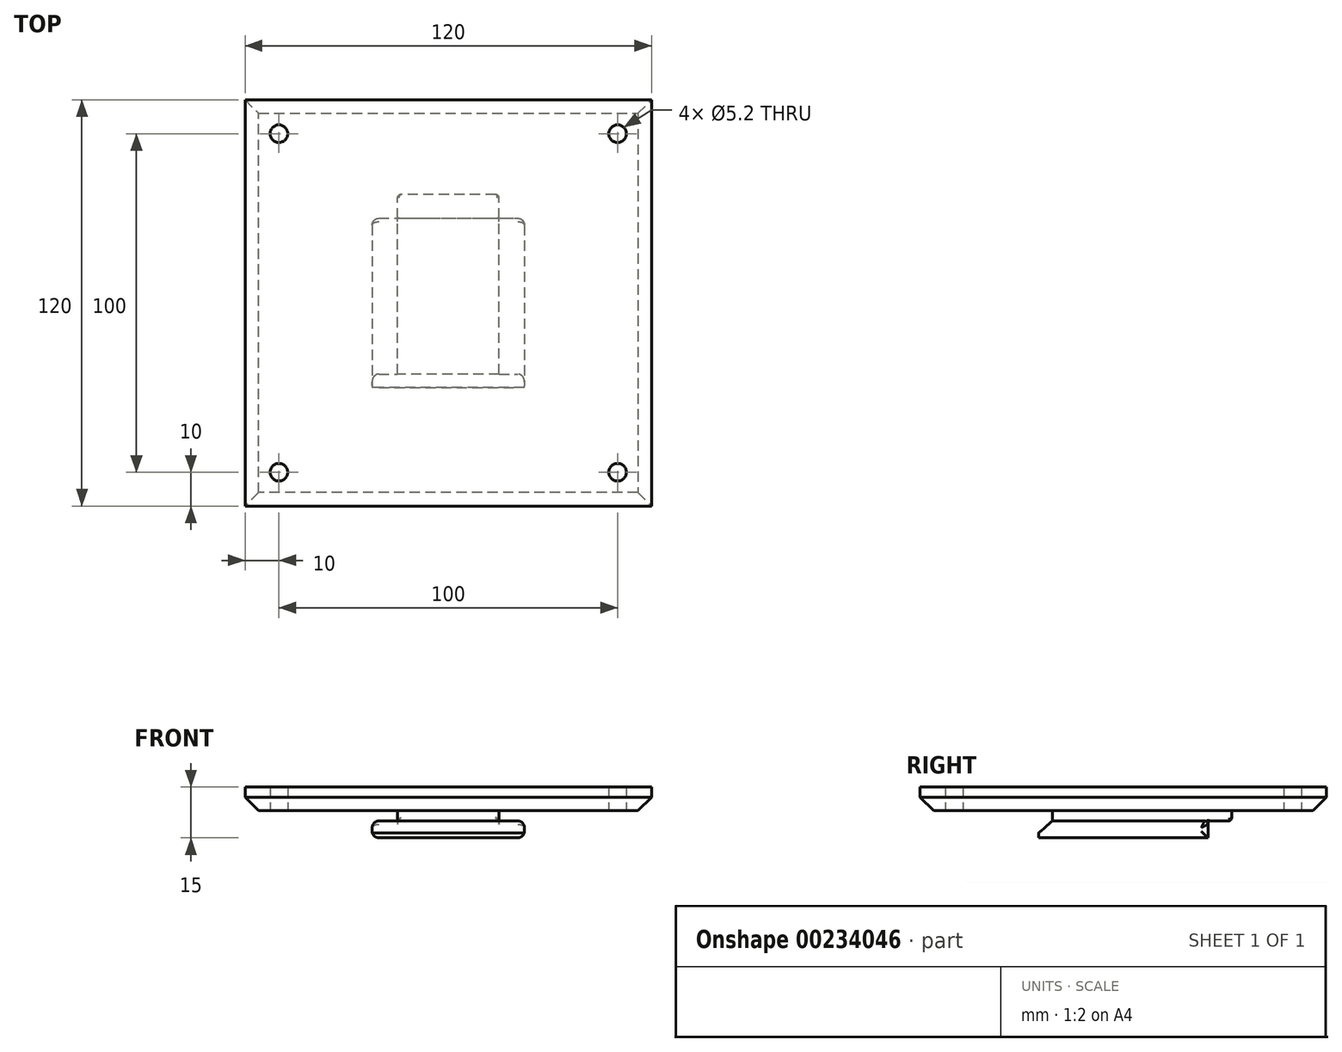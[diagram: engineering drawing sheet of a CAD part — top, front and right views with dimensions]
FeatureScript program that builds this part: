
annotation { "Feature Type Name" : "Feature", "Feature Type Description" : "" }
export const myFeature = defineFeature(function(context is Context, id is Id, definition is map)
    precondition{}
    {
        {
            var Q0;
            Q0=qCreatedBy(makeId("Top.planeOp"),FACE);
            var sketch = newSketch(context, id + "F0", { "sketchPlane" : qUnion([Q0])});
            skLineSegment(sketch, "E0.bottom", {"start": v(-45, 50) * mm, "end": v(0, 50) * mm});
            skLineSegment(sketch, "E0.top", {"start": v(-45, 0) * mm, "end": v(0, 0) * mm});
            skLineSegment(sketch, "E0.left", {"start": v(-45, 50) * mm, "end": v(-45, 0) * mm});
            skLineSegment(sketch, "E0.right", {"start": v(0, 50) * mm, "end": v(0, 0) * mm});
            skSolve(sketch);
        }
        {
            var Q0;
            Q0=makeQuery(id+"F0.imprint","IMPRINT",FACE,{"disambiguationData":[TD([[makeQuery(id+"F0.imprint","IMPRINT",EDGE,{"derivedFrom":sQuery(id+"F0.wireOp",EDGE,"E0.bottom")}),-1.0]])]});
            extrude(context, id + "F1", {"entities" : qUnion([Q0]), "depth" : 5 * mm});
        }
        {
            var Q0;
            Q0=makeQuery(id+"F1.opExtrude","CAP_FACE",FACE,{"disambiguationData":[OSD([sQuery(id+"F0.wireOp",EDGE,"E0.bottom"),sQuery(id+"F0.wireOp",EDGE,"E0.top"),sQuery(id+"F0.wireOp",EDGE,"E0.left"),sQuery(id+"F0.wireOp",EDGE,"E0.right")])],"isStart":false});
            var sketch = newSketch(context, id + "F2", { "sketchPlane" : qUnion([Q0])});
            skLineSegment(sketch, "E1.bottom", {"start": v(-7.5, 4) * mm, "end": v(-37.5, 4) * mm});
            skLineSegment(sketch, "E1.top", {"start": v(-7.5, 57) * mm, "end": v(-37.5, 57) * mm});
            skLineSegment(sketch, "E1.left", {"start": v(-7.5, 4) * mm, "end": v(-7.5, 57) * mm});
            skLineSegment(sketch, "E1.right", {"start": v(-37.5, 4) * mm, "end": v(-37.5, 57) * mm});
            skSolve(sketch);
        }
        {
            var Q0;
            {var subQ0=sQuery(id+"F2.wireOp",EDGE,"E1.top");Q0=makeQuery(id+"F2.imprint","IMPRINT",FACE,{"disambiguationData":[TD([[makeQuery(id+"F2.imprint","IMPRINT",EDGE,{"derivedFrom":subQ0}),1.0]])]});}
            var Q1;
            {var subQ0=sQuery(id+"F2.wireOp",EDGE,"E1.bottom");Q1=makeQuery(id+"F2.imprint","IMPRINT",FACE,{"disambiguationData":[TD([[makeQuery(id+"F2.imprint","IMPRINT",EDGE,{"derivedFrom":subQ0}),-1.0]])]});}
            extrude(context, id + "F3", {"entities" : qUnion([Q0, Q1]), "operationType" : NewBodyOperationType.ADD, "depth" : 3 * mm});
        }
        {
            var Q0;
            Q0=makeQuery(id+"F3.opExtrude","CAP_FACE",FACE,{"disambiguationData":[OSD([sQuery(id+"F2.wireOp",EDGE,"E1.bottom"),sQuery(id+"F2.wireOp",EDGE,"E1.top"),sQuery(id+"F2.wireOp",EDGE,"E1.left"),sQuery(id+"F2.wireOp",EDGE,"E1.right")])],"isStart":false});
            var sketch = newSketch(context, id + "F4", { "sketchPlane" : qUnion([Q0])});
            skLineSegment(sketch, "E2.bottom", {"start": v(-82.5, 85) * mm, "end": v(37.5, 85) * mm});
            skLineSegment(sketch, "E2.top", {"start": v(-82.5, -35) * mm, "end": v(37.5, -35) * mm});
            skLineSegment(sketch, "E2.left", {"start": v(-82.5, 85) * mm, "end": v(-82.5, -35) * mm});
            skLineSegment(sketch, "E2.right", {"start": v(37.5, 85) * mm, "end": v(37.5, -35) * mm});
            skLineSegment(sketch, "E3", {"start": v(-22.5, 85) * mm, "end": v(-22.5, -35) * mm, "construction": true});
            skLineSegment(sketch, "E4", {"start": v(-82.5, 25) * mm, "end": v(37.5, 25) * mm, "construction": true});
            skPoint(sketch, "E5", {"position": v(-22.5, 25) * mm});
            skLineSegment(sketch, "E6.bottom", {"start": v(27.5, 75) * mm, "end": v(-72.5, 75) * mm, "construction": true});
            skLineSegment(sketch, "E6.top", {"start": v(27.5, -25) * mm, "end": v(-72.5, -25) * mm, "construction": true});
            skLineSegment(sketch, "E6.left", {"start": v(27.5, 75) * mm, "end": v(27.5, -25) * mm, "construction": true});
            skLineSegment(sketch, "E6.right", {"start": v(-72.5, 75) * mm, "end": v(-72.5, -25) * mm, "construction": true});
            skPoint(sketch, "E7", {"position": v(-72.5, 75) * mm});
            skPoint(sketch, "E8", {"position": v(27.5, 75) * mm});
            skPoint(sketch, "E9", {"position": v(27.5, -25) * mm});
            skPoint(sketch, "E10", {"position": v(-72.5, -25) * mm});
            skSolve(sketch);
        }
        {
            var Q0;
            Q0=makeQuery(id+"F4.imprint","IMPRINT",FACE,{"disambiguationData":[TD([[makeQuery(id+"F4.imprint","IMPRINT",EDGE,{"derivedFrom":sQuery(id+"F4.wireOp",EDGE,"E2.bottom")}),-1.0]])]});
            var Q1;
            Q1=makeQuery(id+"F4.imprint","IMPRINT",FACE,{"disambiguationData":[TD([[makeQuery(id+"F4.imprint","IMPRINT",EDGE,{"derivedFrom":makeQuery(id+"F3.opExtrude","CAP_EDGE",EDGE,{"disambiguationData":[OSD([sQuery(id+"F2.wireOp",EDGE,"E1.bottom")])],"isStart":false})}),-1.0]])]});
            extrude(context, id + "F5", {"entities" : qUnion([Q0, Q1]), "operationType" : NewBodyOperationType.ADD, "depth" : 7 * mm});
        }
        {
            var Q0;
            Q0=sQuery(id+"F4.wireOp",VERTEX,"E10");
            var Q1;
            Q1=sQuery(id+"F4.wireOp",VERTEX,"E9");
            var Q2;
            Q2=sQuery(id+"F4.wireOp",VERTEX,"E8");
            var Q3;
            Q3=sQuery(id+"F4.wireOp",VERTEX,"E7");
            var Q4;
            Q4=makeQuery(id+"F1.opExtrude","SWEPT_BODY",BODY,{"disambiguationData":[OSD([sQuery(id+"F0.wireOp",EDGE,"E0.bottom"),sQuery(id+"F0.wireOp",EDGE,"E0.top"),sQuery(id+"F0.wireOp",EDGE,"E0.left"),sQuery(id+"F0.wireOp",EDGE,"E0.right")])]});
            hole(context, id + "F6", {"style" : HoleStyle.SIMPLE, "endStyle" : HoleEndStyle.THROUGH, "oppositeDirection" : true, "holeDiameter" : 5.2 * mm, "startFromSketch" : true, "locations" : qUnion([Q0, Q1, Q2, Q3]), "scope" : qUnion([Q4]), "isTappedThrough" : true});
        }
        {
            var Q0;
            Q0=makeQuery(id+"F1.opExtrude","CAP_EDGE",EDGE,{"disambiguationData":[OSD([sQuery(id+"F0.wireOp",EDGE,"E0.top")])],"isStart":false});
            chamfer(context, id + "F7", {"entities" : qUnion([Q0]), "chamferType" : ChamferType.TWO_OFFSETS, "width1" : 4 * mm, "oppositeDirection" : false, "width2" : 3.5 * mm, "tangentPropagation" : true});
        }
        {
            var Q0;
            Q0=makeQuery(id+"F3.opExtrude","CAP_EDGE",EDGE,{"disambiguationData":[OSD([sQuery(id+"F2.wireOp",EDGE,"E1.bottom")])],"isStart":false});
            var Q1;
            Q1=makeQuery(id+"F3.opExtrude","CAP_EDGE",EDGE,{"disambiguationData":[OSD([sQuery(id+"F2.wireOp",EDGE,"E1.right")])],"isStart":false});
            var Q2;
            Q2=makeQuery(id+"F3.opExtrude","CAP_EDGE",EDGE,{"disambiguationData":[OSD([sQuery(id+"F2.wireOp",EDGE,"E1.left")])],"isStart":false});
            var Q3;
            {var subQ0=sQuery(id+"F2.wireOp",EDGE,"E1.right");Q3=makeQuery(id+"F3.boolean.opBoolean","SPLIT",EDGE,{"disambiguationData":[topologyDisambiguationEdgeConnected([makeQuery(id+"F1.opExtrude","CAP_FACE",FACE,{"disambiguationData":[OSD([sQuery(id+"F0.wireOp",EDGE,"E0.bottom"),sQuery(id+"F0.wireOp",EDGE,"E0.top"),sQuery(id+"F0.wireOp",EDGE,"E0.left"),sQuery(id+"F0.wireOp",EDGE,"E0.right")])],"isStart":false})])],"derivedFrom":makeQuery(id+"F3.opExtrude","CAP_EDGE",EDGE,{"disambiguationData":[OSD([subQ0])],"isStart":true})});}
            var Q4;
            Q4=makeQuery(id+"F3.opExtrude","CAP_EDGE",EDGE,{"disambiguationData":[OSD([sQuery(id+"F2.wireOp",EDGE,"E1.top")])],"isStart":false});
            var Q5;
            {var subQ0=sQuery(id+"F2.wireOp",EDGE,"E1.left");Q5=makeQuery(id+"F3.boolean.opBoolean","SPLIT",EDGE,{"disambiguationData":[topologyDisambiguationEdgeConnected([makeQuery(id+"F1.opExtrude","CAP_FACE",FACE,{"disambiguationData":[OSD([sQuery(id+"F0.wireOp",EDGE,"E0.bottom"),sQuery(id+"F0.wireOp",EDGE,"E0.top"),sQuery(id+"F0.wireOp",EDGE,"E0.left"),sQuery(id+"F0.wireOp",EDGE,"E0.right")])],"isStart":false})])],"derivedFrom":makeQuery(id+"F3.opExtrude","CAP_EDGE",EDGE,{"disambiguationData":[OSD([subQ0])],"isStart":true})});}
            fillet(context, id + "F8", {"entities" : qUnion([Q0, Q1, Q2, Q3, Q4, Q5]), "radius" : 0.5 * mm, "tangentPropagation" : true, "allowEdgeOverflow" : false});
        }
        {
            var Q0;
            {var subQ0=sQuery(id+"F0.wireOp",EDGE,"E0.bottom");Q0=makeQuery(id+"F3.boolean.opBoolean","SPLIT",EDGE,{"disambiguationData":[topologyDisambiguationEdgeConnected([makeQuery(id+"F1.opExtrude","SWEPT_FACE",FACE,{"disambiguationData":[OSD([subQ0])]}),makeQuery(id+"F3.opExtrude","CAP_FACE",FACE,{"disambiguationData":[OSD([sQuery(id+"F2.wireOp",EDGE,"E1.bottom"),sQuery(id+"F2.wireOp",EDGE,"E1.top"),sQuery(id+"F2.wireOp",EDGE,"E1.left"),sQuery(id+"F2.wireOp",EDGE,"E1.right")])],"isStart":true})])],"derivedFrom":makeQuery(id+"F1.opExtrude","CAP_EDGE",EDGE,{"disambiguationData":[OSD([subQ0])],"isStart":false})});}
            var Q1;
            Q1=makeQuery(id+"F3.opExtrude","CAP_EDGE",EDGE,{"disambiguationData":[OSD([sQuery(id+"F2.wireOp",EDGE,"E1.top")])],"isStart":true});
            fillet(context, id + "F9", {"entities" : qUnion([Q0, Q1]), "radius" : 1 * mm, "tangentPropagation" : true, "allowEdgeOverflow" : false});
        }
        {
            var Q0;
            Q0=makeQuery(id+"F5.opExtrude","CAP_EDGE",EDGE,{"disambiguationData":[OSD([sQuery(id+"F4.wireOp",EDGE,"E2.right")])],"isStart":true});
            var Q1;
            Q1=makeQuery(id+"F5.opExtrude","CAP_EDGE",EDGE,{"disambiguationData":[OSD([sQuery(id+"F4.wireOp",EDGE,"E2.bottom")])],"isStart":true});
            var Q2;
            Q2=makeQuery(id+"F5.opExtrude","CAP_EDGE",EDGE,{"disambiguationData":[OSD([sQuery(id+"F4.wireOp",EDGE,"E2.left")])],"isStart":true});
            var Q3;
            Q3=makeQuery(id+"F5.opExtrude","CAP_EDGE",EDGE,{"disambiguationData":[OSD([sQuery(id+"F4.wireOp",EDGE,"E2.top")])],"isStart":true});
            chamfer(context, id + "F10", {"entities" : qUnion([Q0, Q1, Q2, Q3]), "width" : 4 * mm, "tangentPropagation" : true});
        }
        {
            var Q0;
            Q0=makeQuery(id+"F1.opExtrude","CAP_EDGE",EDGE,{"disambiguationData":[OSD([sQuery(id+"F0.wireOp",EDGE,"E0.left")])],"isStart":true});
            var Q1;
            Q1=makeQuery(id+"F1.opExtrude","CAP_EDGE",EDGE,{"disambiguationData":[OSD([sQuery(id+"F0.wireOp",EDGE,"E0.left")])],"isStart":false});
            var Q2;
            Q2=makeQuery(id+"F1.opExtrude","CAP_EDGE",EDGE,{"disambiguationData":[OSD([sQuery(id+"F0.wireOp",EDGE,"E0.right")])],"isStart":true});
            var Q3;
            Q3=makeQuery(id+"F1.opExtrude","CAP_EDGE",EDGE,{"disambiguationData":[OSD([sQuery(id+"F0.wireOp",EDGE,"E0.right")])],"isStart":false});
            fillet(context, id + "F11", {"entities" : qUnion([Q0, Q1, Q2, Q3]), "radius" : 2 * mm, "tangentPropagation" : true, "allowEdgeOverflow" : false});
        }
    });
